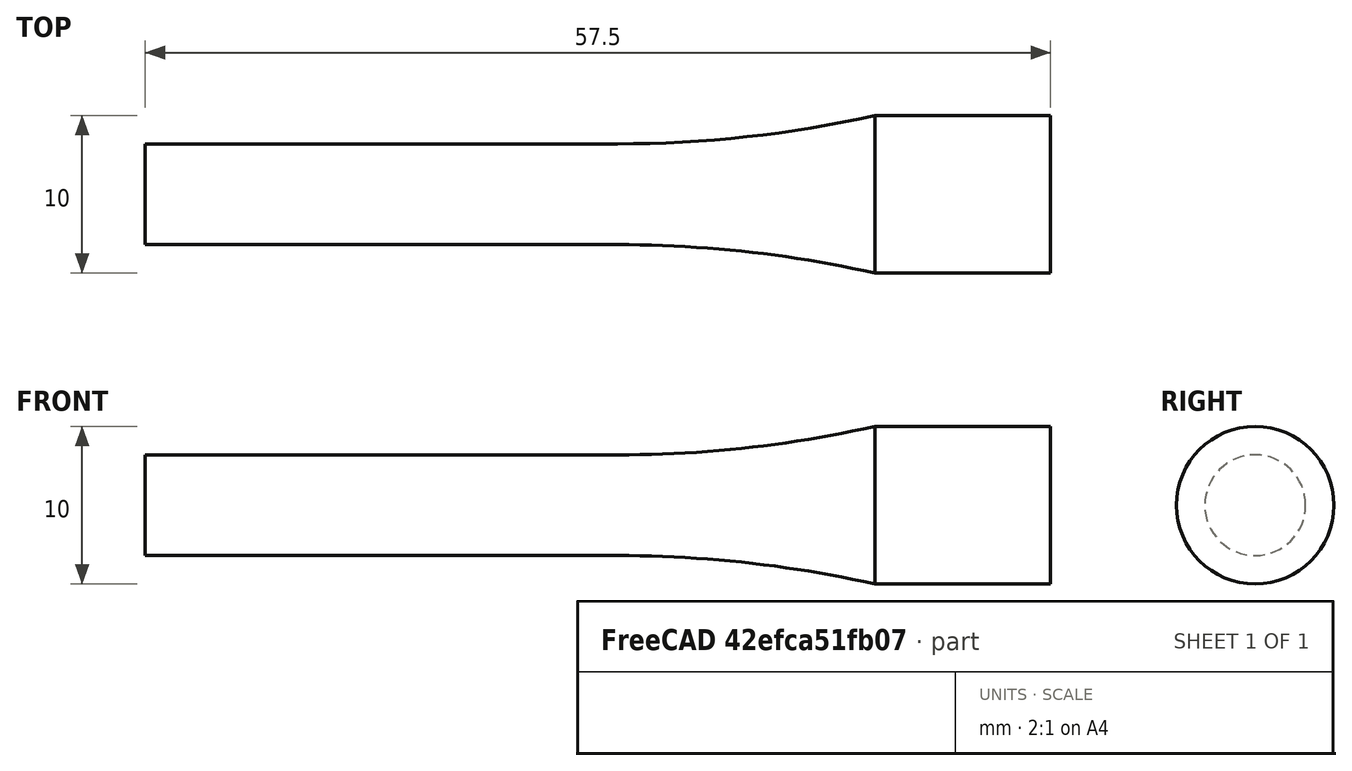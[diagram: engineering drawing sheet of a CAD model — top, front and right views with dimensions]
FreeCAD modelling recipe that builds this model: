
FCSTD DOCUMENT  (FreeCAD 0.19R)
Label: E8_D6_4
License: All rights reserved
LicenseURL: http://en.wikipedia.org/wiki/All_rights_reserved
objects: Sketcher::SketchObject×1, PartDesign::Revolution×1, PartDesign::Body×1
note: 4 computed .brp shape members not serialized (recipe doc carries the construction recipe); baked Part::Feature solids carry a one-line shape summary decoded from their .brp

FEATURE [Sketcher::SketchObject] Sketch
  FullyConstrained = false
  MapMode = 5
  Support = -> [XY_Plane]
  sketch-geometry (10):
    g0: GeomPoint X=0 Y=3.2 Z=0
    g1: GeomPoint X=30 Y=3.2 Z=0
    g2: GeomPoint X=92.5486 Y=36.3931 Z=0
    g3: GeomPoint X=57.5 Y=0 Z=0
    g4: LineSegment StartX=0 StartY=0 StartZ=0 EndX=0 EndY=3.2 EndZ=0
    g5: LineSegment StartX=0 StartY=3.2 StartZ=0 EndX=30 EndY=3.2 EndZ=0
    g6: LineSegment StartX=57.5 StartY=5 StartZ=0 EndX=57.5 EndY=0 EndZ=0
    g7: LineSegment StartX=57.5 StartY=0 StartZ=0 EndX=0 EndY=0 EndZ=0
    g8: ArcOfCircle CenterX=30 CenterY=78.2 CenterZ=0 NormalX=0 NormalY=0 NormalZ=1 AngleXU=0 Radius=75 StartAngle=4.71239 EndAngle=4.93192
    g9: LineSegment StartX=46.3328 StartY=5 StartZ=0 EndX=57.5 EndY=5 EndZ=0
  constraints (19):
    c: Coincident(g4,g-1)
    c: Coincident(g4,g0)
    c: Vertical(g4)
    c: Coincident(g5,g4)
    c: Horizontal(g5)
    c: Coincident(g6,g3)
    c: Vertical(g6)
    c: Coincident(g7,g6)
    c: Coincident(g7,g4)
    c: Horizontal(g7)
    c: DistanceY(g4,g4) = 3.2
    c: DistanceX(g7,g7) = 57.5
    c: Tangent(g5,g8) = -1.5708
    c: DistanceX(g5,g5) = 30
    c: Horizontal(g9)
    c: Coincident(g9,g6)
    c: Coincident(g9,g8)
    c: Radius(g8) = 75
    c: DistanceY(g6,g6) = 5
FEATURE [PartDesign::Revolution] Revolution
  Angle = 360
  Axis = (1,0,0)
  Base = (0,0,0)
  Profile = -> Sketch
  ReferenceAxis = -> Sketch [H_Axis]
FEATURE [PartDesign::Body] Body
  Group = -> [Sketch,Revolution]
  Origin = -> Origin
  Tip = -> Revolution
